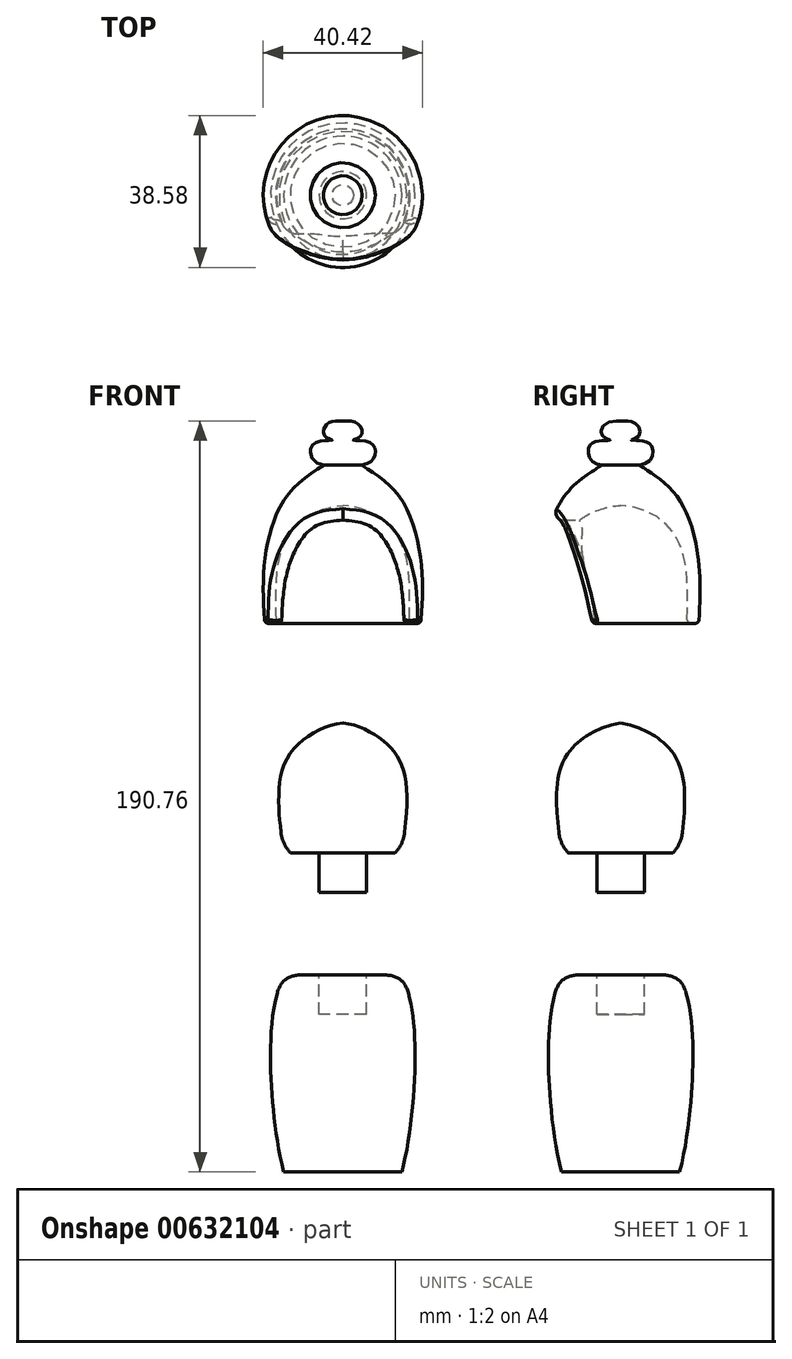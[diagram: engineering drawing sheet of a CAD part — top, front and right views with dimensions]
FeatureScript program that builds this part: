
annotation { "Feature Type Name" : "Feature", "Feature Type Description" : "" }
export const myFeature = defineFeature(function(context is Context, id is Id, definition is map)
    precondition{}
    {
        {
            var Q0;
            Q0=qCreatedBy(makeId("Front.planeOp"),FACE);
            var sketch = newSketch(context, id + "F0", { "sketchPlane" : qUnion([Q0])});
            skLineSegment(sketch, "E0", {"start": v(0, 176.63) * mm, "end": v(0, -19) * mm, "construction": true});
            skLineSegment(sketch, "E1", {"start": v(0, -24.2) * mm, "end": v(15, -24.2) * mm});
            skLineSegment(sketch, "E2", {"start": v(6, 25.8) * mm, "end": v(15, 25.8) * mm});
            skFitSpline(sketch, "E3", {"points": [v(15, 25.8) * mm, v(18.3, 9.25) * mm, v(15, -24.2) * mm], "startDerivative": vector(13.35, -28.33) * mm, "endDerivative": vector(-12.15, -45.61) * mm});
            skLineSegment(sketch, "E4", {"start": v(6, 25.8) * mm, "end": v(6, 15.8) * mm});
            skLineSegment(sketch, "E5", {"start": v(6, 15.8) * mm, "end": v(0, 15.8) * mm});
            skLineSegment(sketch, "E6", {"start": v(0, 15.8) * mm, "end": v(0, -24.2) * mm});
            skLineSegment(sketch, "E7", {"start": v(0, 46.83) * mm, "end": v(6, 46.83) * mm});
            skLineSegment(sketch, "E8", {"start": v(6, 46.83) * mm, "end": v(6, 56.83) * mm});
            skLineSegment(sketch, "E9", {"start": v(6, 56.83) * mm, "end": v(13.27, 56.83) * mm});
            skFitSpline(sketch, "E10", {"points": [v(15, 56.83) * mm, v(15, 79.02) * mm, v(9.66, 85.82) * mm, v(0, 89.83) * mm], "startDerivative": vector(11.54, 76.11) * mm, "endDerivative": vector(-35.15, 3.35) * mm});
            skLineSegment(sketch, "E11", {"start": v(0, 89.83) * mm, "end": v(0, 46.83) * mm});
            skFitSpline(sketch, "E12", {"points": [v(16.85, 115.14) * mm, v(15, 135.11) * mm, v(9.66, 141.91) * mm, v(0, 145.14) * mm], "startDerivative": vector(2.73, 80.62) * mm, "endDerivative": vector(-35.15, 3.35) * mm});
            skLineSegment(sketch, "E13", {"start": v(16.85, 115.14) * mm, "end": v(19.85, 115.14) * mm});
            skFitSpline(sketch, "E14", {"points": [v(19.85, 115.14) * mm, v(19.85, 131) * mm, v(14.5, 147.18) * mm, v(4.75, 155.34) * mm], "startDerivative": vector(2.8, 45.36) * mm, "endDerivative": vector(-35.14, 22.05) * mm});
            skFitSpline(sketch, "E15", {"points": [v(4.75, 155.34) * mm, v(8.2, 158.15) * mm, v(6.92, 161.07) * mm, v(2.68, 161.73) * mm, v(4.57, 162.72) * mm, v(4.05, 165.73) * mm, v(0, 166.52) * mm], "startDerivative": vector(38.47, 6.35) * mm, "endDerivative": vector(-22.75, -1.6) * mm});
            skLineSegment(sketch, "E16", {"start": v(0, 166.52) * mm, "end": v(0, 145.14) * mm});
            skLineSegment(sketch, "E17", {"start": v(13.27, 56.83) * mm, "end": v(15.1, 57.5) * mm});
            skSolve(sketch);
        }
        {
            var Q0;
            Q0=makeQuery(id+"F0.imprint","IMPRINT",FACE,{"disambiguationData":[TD([[makeQuery(id+"F0.imprint","IMPRINT",EDGE,{"derivedFrom":sQuery(id+"F0.wireOp",EDGE,"E1")}),1.0]])]});
            var Q1;
            Q1=sQuery(id+"F0.wireOp",EDGE,"E0");
            revolve(context, id + "F1", {"entities" : qUnion([Q0]), "axis" : qUnion([Q1]), "revolveType" : RevolveType.FULL});
        }
        {
            var Q0;
            Q0=makeQuery(id+"F0.imprint","IMPRINT",FACE,{"disambiguationData":[TD([[makeQuery(id+"F0.imprint","IMPRINT",EDGE,{"derivedFrom":sQuery(id+"F0.wireOp",EDGE,"E7")}),1.0]])]});
            var Q1;
            Q1=sQuery(id+"F0.wireOp",EDGE,"E0");
            revolve(context, id + "F2", {"entities" : qUnion([Q0]), "axis" : qUnion([Q1]), "revolveType" : RevolveType.FULL});
        }
        {
            var Q0;
            Q0=makeQuery(id+"F0.imprint","IMPRINT",FACE,{"disambiguationData":[TD([[makeQuery(id+"F0.imprint","IMPRINT",EDGE,{"derivedFrom":sQuery(id+"F0.wireOp",EDGE,"E12")}),-1.0]])]});
            var Q1;
            Q1=sQuery(id+"F0.wireOp",EDGE,"E0");
            revolve(context, id + "F3", {"entities" : qUnion([Q0]), "axis" : qUnion([Q1]), "revolveType" : RevolveType.FULL});
        }
        {
            var Q0;
            Q0=qCreatedBy(makeId("Front.planeOp"),FACE);
            var sketch = newSketch(context, id + "F4", { "sketchPlane" : qUnion([Q0])});
            skLineSegment(sketch, "E18.0", {"start": v(-19.85, 115.14) * mm, "end": v(19.85, 115.14) * mm});
            skFitSpline(sketch, "E19", {"points": [v(-15.1, 115.14) * mm, v(-13.83, 129.1) * mm, v(-7.73, 139.32) * mm, v(0, 141.38) * mm], "startDerivative": vector(0.14, 37.78) * mm, "endDerivative": vector(28.89, 2.35) * mm});
            skLineSegment(sketch, "E20", {"start": v(0, 141.38) * mm, "end": v(0, 109.75) * mm, "construction": true});
            skFitSpline(sketch, "E21.MirrorCS", {"points": [v(15.1, 115.14) * mm, v(13.83, 129.1) * mm, v(7.73, 139.32) * mm, v(0, 141.38) * mm], "startDerivative": vector(-0.14, 37.78) * mm, "endDerivative": vector(-28.89, 2.35) * mm});
            skLineSegment(sketch, "E22", {"start": v(-15.1, 115.14) * mm, "end": v(15.1, 115.14) * mm});
            skSolve(sketch);
        }
        {
            var Q0;
            Q0=makeQuery(id+"F4.imprint","IMPRINT",FACE,{"disambiguationData":[TD([[makeQuery(id+"F4.imprint","IMPRINT",EDGE,{"derivedFrom":sQuery(id+"F4.wireOp",EDGE,"E19")}),-1.0]])]});
            extrude(context, id + "F5", {"entities" : qUnion([Q0]), "operationType" : NewBodyOperationType.REMOVE, "depth" : 25 * mm, "offsetDistance" : 25 * mm});
        }
        {
            var Q0;
            Q0=makeQuery(id+"F5.boolean.opBoolean","INTERSECT",EDGE,{"derivedFrom":[makeQuery(id+"F3.opRevolve","SWEPT_FACE",FACE,{"disambiguationData":[OSD([sQuery(id+"F0.wireOp",EDGE,"E14")])]}),makeQuery(id+"F5.opExtrude","SWEPT_FACE",FACE,{"disambiguationData":[OSD([sQuery(id+"F4.wireOp",EDGE,"E21.MirrorCS")])]})]});
            var Q1;
            Q1=makeQuery(id+"F5.boolean.opBoolean","INTERSECT",EDGE,{"derivedFrom":[makeQuery(id+"F3.opRevolve","SWEPT_FACE",FACE,{"disambiguationData":[OSD([sQuery(id+"F0.wireOp",EDGE,"E14")])]}),makeQuery(id+"F5.opExtrude","SWEPT_FACE",FACE,{"disambiguationData":[OSD([sQuery(id+"F4.wireOp",EDGE,"E19")])]})]});
            fillet(context, id + "F6", {"entities" : qUnion([Q0, Q1]), "radius" : 2 * mm, "tangentPropagation" : true, "allowEdgeOverflow" : false});
        }
        {
            var Q0;
            Q0=makeQuery(id+"F3.opRevolve","SWEPT_EDGE",EDGE,{"disambiguationData":[OSD([sQuery(id+"F0.wireOp",EDGE,"E12"),sQuery(id+"F0.wireOp",EDGE,"E13")])]});
            var Q1;
            Q1=makeQuery(id+"F3.opRevolve","SWEPT_EDGE",EDGE,{"disambiguationData":[OSD([sQuery(id+"F0.wireOp",EDGE,"E13"),sQuery(id+"F0.wireOp",EDGE,"E14")])]});
            fillet(context, id + "F7", {"entities" : qUnion([Q0, Q1]), "radius" : 1 * mm, "tangentPropagation" : true, "allowEdgeOverflow" : false});
        }
        {
            var Q0;
            Q0=makeQuery(id+"F1.opRevolve","SWEPT_EDGE",EDGE,{"disambiguationData":[OSD([sQuery(id+"F0.wireOp",EDGE,"E2"),sQuery(id+"F0.wireOp",EDGE,"E3")])]});
            fillet(context, id + "F8", {"entities" : qUnion([Q0]), "radius" : 6.14 * mm, "tangentPropagation" : true, "rho" : 0.5, "crossSection" : FilletCrossSection.CONIC, "allowEdgeOverflow" : false});
        }
        {
            var Q0;
            Q0=makeQuery(id+"F2.opRevolve","SWEPT_EDGE",EDGE,{"disambiguationData":[OSD([sQuery(id+"F0.wireOp",EDGE,"E10"),sQuery(id+"F0.wireOp",EDGE,"E17")])]});
            fillet(context, id + "F9", {"entities" : qUnion([Q0]), "radius" : 9.15 * mm, "tangentPropagation" : true, "rho" : 0.5, "crossSection" : FilletCrossSection.CONIC, "allowEdgeOverflow" : false});
        }
    });
